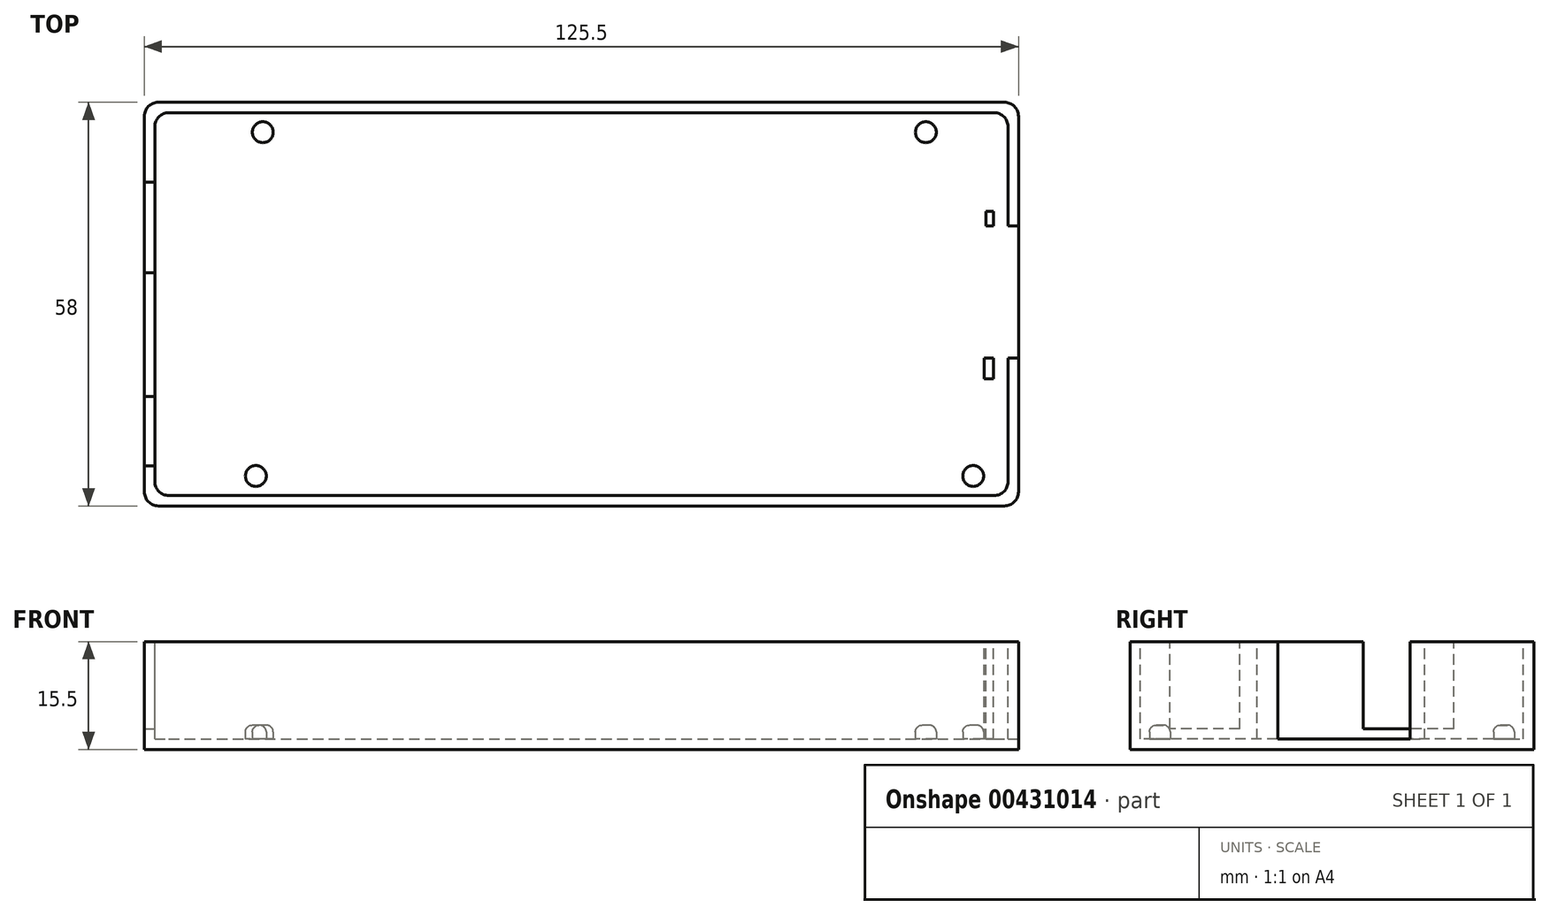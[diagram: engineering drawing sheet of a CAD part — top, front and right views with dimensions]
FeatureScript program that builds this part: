
annotation { "Feature Type Name" : "Feature", "Feature Type Description" : "" }
export const myFeature = defineFeature(function(context is Context, id is Id, definition is map)
    precondition{}
    {
        {
            var Q0;
            Q0=qCreatedBy(makeId("Top.planeOp"),FACE);
            var sketch = newSketch(context, id + "F0", { "sketchPlane" : qUnion([Q0])});
            skLineSegment(sketch, "E0.bottom", {"start": v(-52.22, 34.64) * mm, "end": v(73.28, 34.64) * mm});
            skLineSegment(sketch, "E0.top", {"start": v(-52.22, -23.36) * mm, "end": v(73.28, -23.36) * mm});
            skLineSegment(sketch, "E0.left", {"start": v(-52.22, 34.64) * mm, "end": v(-52.22, -23.36) * mm});
            skLineSegment(sketch, "E0.right", {"start": v(73.28, 34.64) * mm, "end": v(73.28, -23.36) * mm});
            skSolve(sketch);
        }
        {
            var Q0;
            Q0 = qSketchRegion(id + "F0", true);
            extrude(context, id + "F1", {"entities" : qUnion([Q0]), "depth" : 15.5 * mm});
        }
        {
            var Q0;
            Q0=makeQuery(id+"F1.opExtrude","CAP_FACE",FACE,{"disambiguationData":[OSD([sQuery(id+"F0.wireOp",EDGE,"E0.bottom"),sQuery(id+"F0.wireOp",EDGE,"E0.top"),sQuery(id+"F0.wireOp",EDGE,"E0.left"),sQuery(id+"F0.wireOp",EDGE,"E0.right")])],"isStart":false});
            var sketch = newSketch(context, id + "F2", { "sketchPlane" : qUnion([Q0])});
            skLineSegment(sketch, "E1.bottom", {"start": v(-50.72, 33.14) * mm, "end": v(71.78, 33.14) * mm});
            skLineSegment(sketch, "E1.top", {"start": v(-50.72, -21.86) * mm, "end": v(71.78, -21.86) * mm});
            skLineSegment(sketch, "E1.left", {"start": v(-50.72, 33.14) * mm, "end": v(-50.72, -21.86) * mm});
            skLineSegment(sketch, "E1.right", {"start": v(71.78, 33.14) * mm, "end": v(71.78, -21.86) * mm});
            skSolve(sketch);
        }
        {
            var Q0;
            Q0 = qSketchRegion(id + "F2", true);
            extrude(context, id + "F3", {"entities" : qUnion([Q0]), "operationType" : NewBodyOperationType.REMOVE, "oppositeDirection" : true, "depth" : 14 * mm});
        }
        {
            var Q0;
            Q0=makeQuery(id+"F1.opExtrude","CAP_FACE",FACE,{"disambiguationData":[OSD([sQuery(id+"F0.wireOp",EDGE,"E0.bottom"),sQuery(id+"F0.wireOp",EDGE,"E0.top"),sQuery(id+"F0.wireOp",EDGE,"E0.left"),sQuery(id+"F0.wireOp",EDGE,"E0.right")])],"isStart":false});
            var sketch = newSketch(context, id + "F4", { "sketchPlane" : qUnion([Q0])});
            skLineSegment(sketch, "E2.bottom", {"start": v(-52.22, 23.14) * mm, "end": v(-50.72, 23.14) * mm});
            skLineSegment(sketch, "E2.top", {"start": v(-52.22, 10.14) * mm, "end": v(-50.72, 10.14) * mm});
            skLineSegment(sketch, "E2.left", {"start": v(-52.22, 23.14) * mm, "end": v(-52.22, 10.14) * mm});
            skLineSegment(sketch, "E2.right", {"start": v(-50.72, 23.14) * mm, "end": v(-50.72, 10.14) * mm});
            skLineSegment(sketch, "E3.bottom", {"start": v(-52.22, -7.6) * mm, "end": v(-50.72, -7.6) * mm});
            skLineSegment(sketch, "E3.top", {"start": v(-52.22, -17.6) * mm, "end": v(-50.72, -17.6) * mm});
            skLineSegment(sketch, "E3.left", {"start": v(-52.22, -7.6) * mm, "end": v(-52.22, -17.6) * mm});
            skLineSegment(sketch, "E3.right", {"start": v(-50.72, -7.6) * mm, "end": v(-50.72, -17.6) * mm});
            skSolve(sketch);
        }
        {
            var Q0;
            Q0=makeQuery(id+"F4.imprint","IMPRINT",FACE,{"disambiguationData":[TD([[makeQuery(id+"F4.imprint","IMPRINT",EDGE,{"derivedFrom":sQuery(id+"F4.wireOp",EDGE,"E2.bottom")}),-1.0]])]});
            var Q1;
            Q1=makeQuery(id+"F4.imprint","IMPRINT",FACE,{"disambiguationData":[TD([[makeQuery(id+"F4.imprint","IMPRINT",EDGE,{"derivedFrom":sQuery(id+"F4.wireOp",EDGE,"E3.bottom")}),-1.0]])]});
            extrude(context, id + "F5", {"entities" : qUnion([Q0, Q1]), "operationType" : NewBodyOperationType.REMOVE, "oppositeDirection" : true, "depth" : 12.5 * mm});
        }
        {
            var Q0;
            Q0=makeQuery(id+"F3.boolean.opBoolean","COPY",FACE,{"derivedFrom":makeQuery(id+"F3.opExtrude","CAP_FACE",FACE,{"disambiguationData":[OSD([sQuery(id+"F2.wireOp",EDGE,"E1.bottom"),sQuery(id+"F2.wireOp",EDGE,"E1.top"),sQuery(id+"F2.wireOp",EDGE,"E1.left"),sQuery(id+"F2.wireOp",EDGE,"E1.right")])],"isStart":false})});
            var sketch = newSketch(context, id + "F6", { "sketchPlane" : qUnion([Q0])});
            skCircle(sketch, "E4", {"center": v(-35.22, 30.34) * mm, "radius": 1.5 * mm});
            skCircle(sketch, "E5", {"center": v(-36.22, -19.06) * mm, "radius": 1.5 * mm});
            skCircle(sketch, "E6", {"center": v(66.78, -19.06) * mm, "radius": 1.5 * mm});
            skCircle(sketch, "E7", {"center": v(59.98, 30.34) * mm, "radius": 1.5 * mm});
            skSolve(sketch);
        }
        {
            var Q0;
            Q0=makeQuery(id+"F6.imprint","IMPRINT",FACE,{"disambiguationData":[TD([[makeQuery(id+"F6.imprint","IMPRINT",EDGE,{"derivedFrom":sQuery(id+"F6.wireOp",EDGE,"E4")}),1.0]])]});
            var Q1;
            Q1=makeQuery(id+"F6.imprint","IMPRINT",FACE,{"disambiguationData":[TD([[makeQuery(id+"F6.imprint","IMPRINT",EDGE,{"derivedFrom":sQuery(id+"F6.wireOp",EDGE,"E7")}),1.0]])]});
            var Q2;
            Q2=makeQuery(id+"F6.imprint","IMPRINT",FACE,{"disambiguationData":[TD([[makeQuery(id+"F6.imprint","IMPRINT",EDGE,{"derivedFrom":sQuery(id+"F6.wireOp",EDGE,"E6")}),1.0]])]});
            var Q3;
            Q3=makeQuery(id+"F6.imprint","IMPRINT",FACE,{"disambiguationData":[TD([[makeQuery(id+"F6.imprint","IMPRINT",EDGE,{"derivedFrom":sQuery(id+"F6.wireOp",EDGE,"E5")}),1.0]])]});
            extrude(context, id + "F7", {"entities" : qUnion([Q0, Q1, Q2, Q3]), "operationType" : NewBodyOperationType.ADD, "depth" : 2 * mm});
        }
        {
            var Q0;
            Q0=makeQuery(id+"F7.opExtrude","CAP_FACE",FACE,{"disambiguationData":[OSD([sQuery(id+"F6.wireOp",EDGE,"E4")])],"isStart":false});
            var Q1;
            Q1=makeQuery(id+"F7.opExtrude","CAP_FACE",FACE,{"disambiguationData":[OSD([sQuery(id+"F6.wireOp",EDGE,"E7")])],"isStart":false});
            var Q2;
            Q2=makeQuery(id+"F7.opExtrude","CAP_FACE",FACE,{"disambiguationData":[OSD([sQuery(id+"F6.wireOp",EDGE,"E5")])],"isStart":false});
            var Q3;
            Q3=makeQuery(id+"F7.opExtrude","CAP_FACE",FACE,{"disambiguationData":[OSD([sQuery(id+"F6.wireOp",EDGE,"E6")])],"isStart":false});
            fillet(context, id + "F8", {"entities" : qUnion([Q0, Q1, Q2, Q3]), "radius" : 1 * mm, "tangentPropagation" : true, "allowEdgeOverflow" : false});
        }
        {
            var Q0;
            Q0=makeQuery(id+"F1.opExtrude","SWEPT_EDGE",EDGE,{"disambiguationData":[OSD([sQuery(id+"F0.wireOp",EDGE,"E0.bottom"),sQuery(id+"F0.wireOp",EDGE,"E0.left")])]});
            var Q1;
            Q1=makeQuery(id+"F1.opExtrude","SWEPT_EDGE",EDGE,{"disambiguationData":[OSD([sQuery(id+"F0.wireOp",EDGE,"E0.top"),sQuery(id+"F0.wireOp",EDGE,"E0.left")])]});
            var Q2;
            Q2=makeQuery(id+"F1.opExtrude","SWEPT_EDGE",EDGE,{"disambiguationData":[OSD([sQuery(id+"F0.wireOp",EDGE,"E0.top"),sQuery(id+"F0.wireOp",EDGE,"E0.right")])]});
            var Q3;
            Q3=makeQuery(id+"F1.opExtrude","SWEPT_EDGE",EDGE,{"disambiguationData":[OSD([sQuery(id+"F0.wireOp",EDGE,"E0.bottom"),sQuery(id+"F0.wireOp",EDGE,"E0.right")])]});
            fillet(context, id + "F9", {"entities" : qUnion([Q0, Q1, Q2, Q3]), "radius" : 2 * mm, "tangentPropagation" : true, "allowEdgeOverflow" : false});
        }
        {
            var Q0;
            Q0=makeQuery(id+"F3.boolean.opBoolean","COPY",EDGE,{"derivedFrom":makeQuery(id+"F3.opExtrude","SWEPT_EDGE",EDGE,{"disambiguationData":[OSD([sQuery(id+"F2.wireOp",EDGE,"E1.bottom"),sQuery(id+"F2.wireOp",EDGE,"E1.left")])]})});
            var Q1;
            Q1=makeQuery(id+"F3.boolean.opBoolean","COPY",EDGE,{"derivedFrom":makeQuery(id+"F3.opExtrude","SWEPT_EDGE",EDGE,{"disambiguationData":[OSD([sQuery(id+"F2.wireOp",EDGE,"E1.top"),sQuery(id+"F2.wireOp",EDGE,"E1.right")])]})});
            var Q2;
            Q2=makeQuery(id+"F3.boolean.opBoolean","COPY",EDGE,{"derivedFrom":makeQuery(id+"F3.opExtrude","SWEPT_EDGE",EDGE,{"disambiguationData":[OSD([sQuery(id+"F2.wireOp",EDGE,"E1.bottom"),sQuery(id+"F2.wireOp",EDGE,"E1.right")])]})});
            var Q3;
            Q3=makeQuery(id+"F3.boolean.opBoolean","COPY",EDGE,{"derivedFrom":makeQuery(id+"F3.opExtrude","SWEPT_EDGE",EDGE,{"disambiguationData":[OSD([sQuery(id+"F2.wireOp",EDGE,"E1.top"),sQuery(id+"F2.wireOp",EDGE,"E1.left")])]})});
            fillet(context, id + "F10", {"entities" : qUnion([Q0, Q1, Q2, Q3]), "radius" : 2 * mm, "tangentPropagation" : true, "allowEdgeOverflow" : false});
        }
        {
            var Q0;
            Q0=makeQuery(id+"F2.imprint","IMPRINT",FACE,{"disambiguationData":[TD([[makeQuery(id+"F2.imprint","IMPRINT",EDGE,{"derivedFrom":sQuery(id+"F2.wireOp",EDGE,"E1.bottom")}),1.0]])]});
            var sketch = newSketch(context, id + "F11", { "sketchPlane" : qUnion([Q0])});
            skLineSegment(sketch, "E8.bottom", {"start": v(71.78, 16.86) * mm, "end": v(73.28, 16.86) * mm});
            skLineSegment(sketch, "E8.top", {"start": v(71.78, -2.14) * mm, "end": v(73.28, -2.14) * mm});
            skLineSegment(sketch, "E8.left", {"start": v(71.78, 16.86) * mm, "end": v(71.78, -2.14) * mm});
            skLineSegment(sketch, "E8.right", {"start": v(73.28, 16.86) * mm, "end": v(73.28, -2.14) * mm});
            skSolve(sketch);
        }
        {
            var Q0;
            Q0=makeQuery(id+"F11.imprint","IMPRINT",FACE,{"disambiguationData":[TD([[makeQuery(id+"F11.imprint","IMPRINT",EDGE,{"derivedFrom":sQuery(id+"F11.wireOp",EDGE,"E8.bottom")}),-1.0]])]});
            extrude(context, id + "F12", {"entities" : qUnion([Q0]), "operationType" : NewBodyOperationType.REMOVE, "oppositeDirection" : true, "depth" : 14 * mm});
        }
        {
            var Q0;
            Q0=makeQuery(id+"F2.imprint","IMPRINT",FACE,{"disambiguationData":[TD([[makeQuery(id+"F2.imprint","IMPRINT",EDGE,{"derivedFrom":sQuery(id+"F2.wireOp",EDGE,"E1.bottom")}),-1.0]])]});
            var sketch = newSketch(context, id + "F13", { "sketchPlane" : qUnion([Q0])});
            skLineSegment(sketch, "E9.bottom", {"start": v(69.68, 16.86) * mm, "end": v(68.58, 16.86) * mm});
            skLineSegment(sketch, "E9.top", {"start": v(69.68, 18.97) * mm, "end": v(68.58, 18.97) * mm});
            skLineSegment(sketch, "E9.left", {"start": v(69.68, 16.86) * mm, "end": v(69.68, 18.97) * mm});
            skLineSegment(sketch, "E9.right", {"start": v(68.58, 16.86) * mm, "end": v(68.58, 18.97) * mm});
            skLineSegment(sketch, "E10.bottom", {"start": v(69.68, -2.14) * mm, "end": v(68.37, -2.14) * mm});
            skLineSegment(sketch, "E10.top", {"start": v(69.68, -5.12) * mm, "end": v(68.37, -5.12) * mm});
            skLineSegment(sketch, "E10.left", {"start": v(69.68, -2.14) * mm, "end": v(69.68, -5.12) * mm});
            skLineSegment(sketch, "E10.right", {"start": v(68.37, -2.14) * mm, "end": v(68.37, -5.12) * mm});
            skSolve(sketch);
        }
        {
            var Q0;
            Q0=makeQuery(id+"F13.imprint","IMPRINT",FACE,{"disambiguationData":[TD([[makeQuery(id+"F13.imprint","IMPRINT",EDGE,{"derivedFrom":sQuery(id+"F13.wireOp",EDGE,"E9.bottom")}),-1.0]])]});
            var Q1;
            Q1=makeQuery(id+"F13.imprint","IMPRINT",FACE,{"disambiguationData":[TD([[makeQuery(id+"F13.imprint","IMPRINT",EDGE,{"derivedFrom":sQuery(id+"F13.wireOp",EDGE,"E10.bottom")}),1.0]])]});
            extrude(context, id + "F14", {"entities" : qUnion([Q0, Q1]), "operationType" : NewBodyOperationType.ADD, "oppositeDirection" : true, "depth" : 14 * mm});
        }
    });
